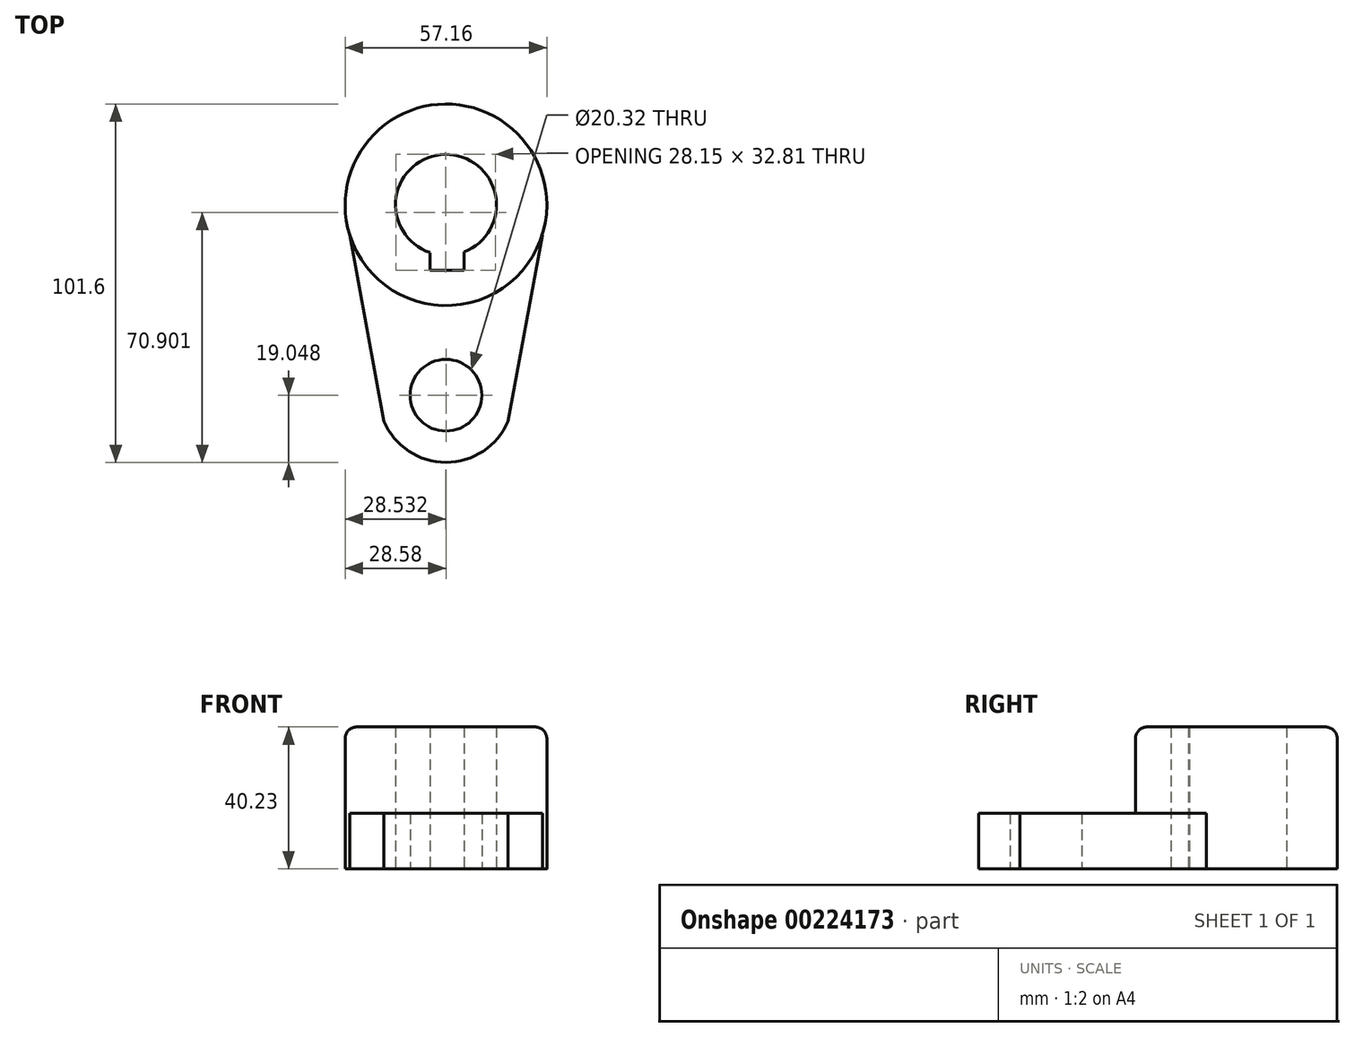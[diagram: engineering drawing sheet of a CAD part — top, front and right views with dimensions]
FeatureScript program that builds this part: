
annotation { "Feature Type Name" : "Feature", "Feature Type Description" : "" }
export const myFeature = defineFeature(function(context is Context, id is Id, definition is map)
    precondition{}
    {
        {
            var Q0;
            Q0=qCreatedBy(makeId("Top.planeOp"),FACE);
            var sketch = newSketch(context, id + "F0", { "sketchPlane" : qUnion([Q0])});
            skCircle(sketch, "E0", {"center": v(0, 32.36) * mm, "radius": 14.29 * mm});
            skCircle(sketch, "E1", {"center": v(0, -21.61) * mm, "radius": 10.16 * mm});
            skCircle(sketch, "E2", {"center": v(0, 32.36) * mm, "radius": 28.58 * mm});
            skCircle(sketch, "E3", {"center": v(0, -21.61) * mm, "radius": 19.05 * mm});
            skLineSegment(sketch, "E4", {"start": v(-27.29, 23.9) * mm, "end": v(-17.57, -28.96) * mm});
            skLineSegment(sketch, "E5", {"start": v(17.57, -28.96) * mm, "end": v(27.29, 23.9) * mm});
            skLineSegment(sketch, "E6", {"start": v(-4.56, 13.83) * mm, "end": v(5.09, 13.83) * mm});
            skLineSegment(sketch, "E7", {"start": v(5.09, 13.83) * mm, "end": v(5.09, 19.01) * mm});
            skLineSegment(sketch, "E8", {"start": v(-4.56, 13.83) * mm, "end": v(-4.56, 18.82) * mm});
            skSolve(sketch);
        }
        {
            var Q0;
            Q0=makeQuery(id+"F0.imprint","IMPRINT",FACE,{"disambiguationData":[TD([[makeQuery(id+"F0.imprint","IMPRINT",EDGE,{"derivedFrom":sQuery(id+"F0.wireOp",EDGE,"E6")}),-1.0]])]});
            extrude(context, id + "F1", {"entities" : qUnion([Q0]), "depth" : 40.23 * mm});
        }
        {
            var Q0;
            {var subQ0=sQuery(id+"F0.wireOp",EDGE,"E4");var subQ1=sQuery(id+"F0.wireOp",EDGE,"E2");var subQ2=makeQuery(id+"F0.imprint","INTERSECT",VERTEX,{"derivedFrom":[subQ1,subQ0]});Q0=makeQuery(id+"F0.imprint","IMPRINT",FACE,{"disambiguationData":[TD([[makeQuery(id+"F0.imprint","IMPRINT",EDGE,{"disambiguationData":[TD([[subQ2,-1.0]])],"derivedFrom":subQ1}),-1.0]])]});}
            var Q1;
            Q1=makeQuery(id+"F0.imprint","IMPRINT",FACE,{"disambiguationData":[TD([[makeQuery(id+"F0.imprint","IMPRINT",EDGE,{"derivedFrom":sQuery(id+"F0.wireOp",EDGE,"E1")}),-1.0]])]});
            extrude(context, id + "F2", {"entities" : qUnion([Q0, Q1]), "operationType" : NewBodyOperationType.ADD, "depth" : 15.77 * mm});
        }
        {
            var Q0;
            Q0=makeQuery(id+"F1.opExtrude","CAP_EDGE",EDGE,{"disambiguationData":[OSD([sQuery(id+"F0.wireOp",EDGE,"E2")])],"isStart":false});
            fillet(context, id + "F3", {"entities" : qUnion([Q0]), "radius" : 3.3 * mm, "tangentPropagation" : true, "allowEdgeOverflow" : false});
        }
    });
